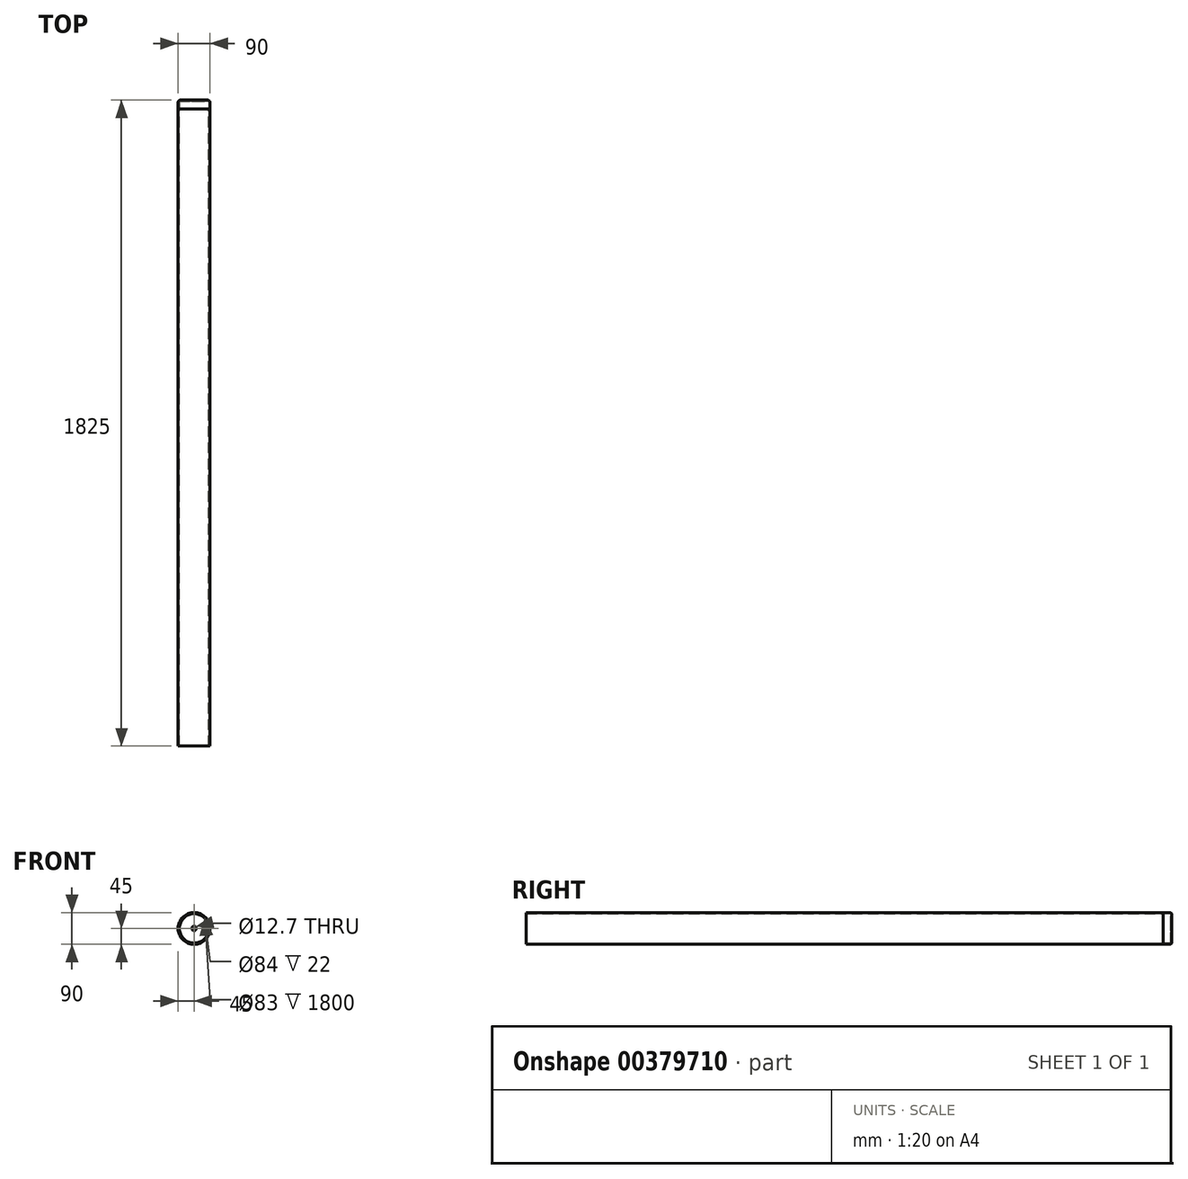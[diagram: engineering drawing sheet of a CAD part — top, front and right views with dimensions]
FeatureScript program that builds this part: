
annotation { "Feature Type Name" : "Feature", "Feature Type Description" : "" }
export const myFeature = defineFeature(function(context is Context, id is Id, definition is map)
    precondition{}
    {
        {
            var Q0;
            Q0=qCreatedBy(makeId("Front.planeOp"),FACE);
            var sketch = newSketch(context, id + "F0", { "sketchPlane" : qUnion([Q0])});
            skCircle(sketch, "E0", {"center": v(0, 0) * mm, "radius": 45 * mm});
            skLineSegment(sketch, "E1", {"start": v(0, 0) * mm, "end": v(45, 0) * mm, "construction": true});
            skCircle(sketch, "E2", {"center": v(0, 0) * mm, "radius": 41.5 * mm});
            skLineSegment(sketch, "E3", {"start": v(0, 0) * mm, "end": v(0, -41.5) * mm, "construction": true});
            skSolve(sketch);
        }
        {
            var Q0;
            Q0 = qSketchRegion(id + "F0", true);
            extrude(context, id + "F1", {"entities" : qUnion([Q0]), "depth" : 1800 * mm});
        }
        {
            var Q0;
            Q0=qCreatedBy(makeId("Front.planeOp"),FACE);
            var sketch = newSketch(context, id + "F2", { "sketchPlane" : qUnion([Q0])});
            skCircle(sketch, "E4", {"center": v(0, 0) * mm, "radius": 45 * mm});
            skLineSegment(sketch, "E5", {"start": v(0, 0) * mm, "end": v(-45, 0) * mm, "construction": true});
            skCircle(sketch, "E6", {"center": v(0, 0) * mm, "radius": 42 * mm});
            skLineSegment(sketch, "E7", {"start": v(0, 0) * mm, "end": v(0, -42) * mm, "construction": true});
            skCircle(sketch, "E8", {"center": v(0, 0) * mm, "radius": 6.35 * mm});
            skLineSegment(sketch, "E9", {"start": v(0, 0) * mm, "end": v(-6.35, 0) * mm, "construction": true});
            skSolve(sketch);
        }
        {
            var Q0;
            Q0=makeQuery(id+"F2.imprint","IMPRINT",FACE,{"disambiguationData":[TD([[makeQuery(id+"F2.imprint","IMPRINT",EDGE,{"derivedFrom":sQuery(id+"F2.wireOp",EDGE,"E6")}),1.0]])]});
            var Q1;
            Q1=makeQuery(id+"F2.imprint","IMPRINT",FACE,{"disambiguationData":[TD([[makeQuery(id+"F2.imprint","IMPRINT",EDGE,{"derivedFrom":sQuery(id+"F2.wireOp",EDGE,"E4")}),1.0]])]});
            extrude(context, id + "F3", {"entities" : qUnion([Q0, Q1]), "oppositeDirection" : true, "depth" : 25 * mm});
        }
        {
            var Q0;
            Q0=makeQuery(id+"F2.imprint","IMPRINT",FACE,{"disambiguationData":[TD([[makeQuery(id+"F2.imprint","IMPRINT",EDGE,{"derivedFrom":sQuery(id+"F2.wireOp",EDGE,"E6")}),1.0]])]});
            extrude(context, id + "F4", {"entities" : qUnion([Q0]), "operationType" : NewBodyOperationType.REMOVE, "oppositeDirection" : true, "depth" : 22 * mm});
        }
        {
            var Q0;
            Q0=makeQuery(id+"F3.opExtrude","CAP_EDGE",EDGE,{"disambiguationData":[OSD([sQuery(id+"F2.wireOp",EDGE,"E4")])],"isStart":false});
            fillet(context, id + "F5", {"entities" : qUnion([Q0]), "radius" : 6 * mm, "tangentPropagation" : true, "allowEdgeOverflow" : false});
        }
        {
            var Q0;
            Q0=makeQuery(id+"F2.imprint","IMPRINT",FACE,{"disambiguationData":[TD([[makeQuery(id+"F2.imprint","IMPRINT",EDGE,{"derivedFrom":sQuery(id+"F2.wireOp",EDGE,"E8")}),1.0]])]});
            extrude(context, id + "F6", {"entities" : qUnion([Q0]), "operationType" : NewBodyOperationType.REMOVE, "oppositeDirection" : true, "depth" : 26 * mm});
        }
    });
